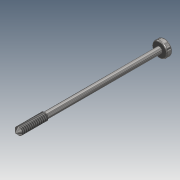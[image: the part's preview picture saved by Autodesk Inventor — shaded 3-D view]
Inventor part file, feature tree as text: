
AUTODESK INVENTOR PART (.ipt)
format: ipt  version: 2017 (Build 210142000, 142)  size: 151,552 bytes
history: native  units: mm
features: sketch x4, chamfer x3, extrude x3, other x1, revolve x1, thread x1, fillet x1, pattern_circular x1
ambient origin geometry x8: Origin, YZ Plane, XZ Plane, XY Plane, X Axis, Y Axis, Z Axis, Center Point
bodies: Body1 (feature_tree)
feature tree (15):
  other  "Твердое тело1"
  revolve  "Вращение1"
  thread  "Резьба1"
  chamfer  "Фаска1"  Distance=20.0mm
  chamfer  "Фаска2"  Distance=1.0mm
  fillet  "Сопряжение1"  Radius=0.8mm
  extrude  "Выдавливание1"  Depth=2.0mm
  extrude  "Выдавливание2"  Depth=0.75mm
  extrude  "Выдавливание3"  Depth=4.0mm
  pattern_circular  "Круговой массив1"  Angle=90.0deg  [1 undecoded]
  chamfer  "Фаска3"  Distance=10.0mm
  sketch  "Эскиз1"
  sketch  "Эскиз2"
  sketch  "Эскиз3"
  sketch  "Эскиз4"
note: 1 required parameter value undecoded (feature->parameter linkage not recoverable at this tier; creation-order binding heuristic only, values carry confidence <= 0.55)
